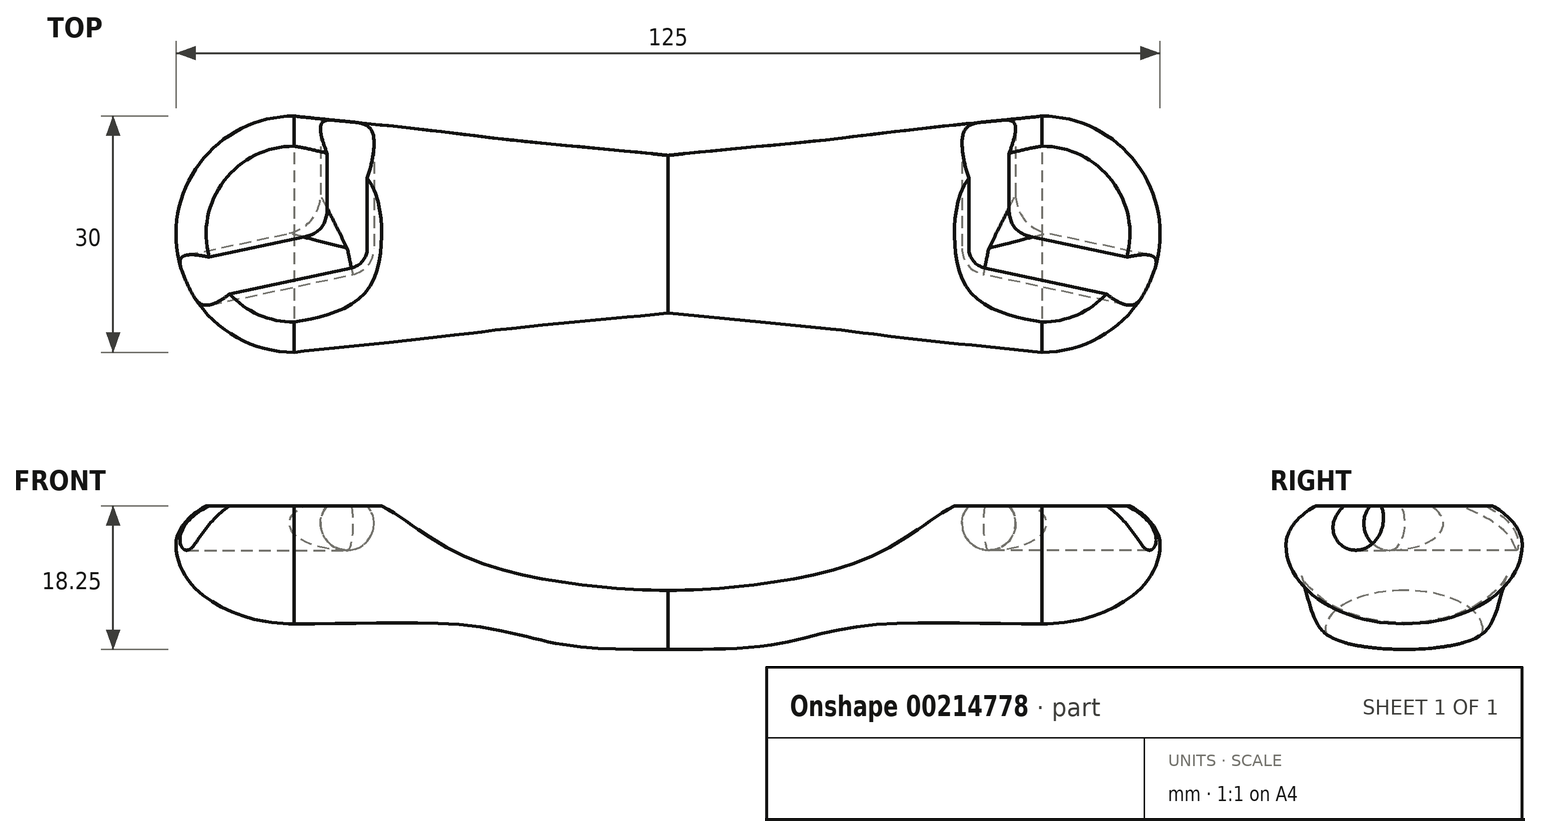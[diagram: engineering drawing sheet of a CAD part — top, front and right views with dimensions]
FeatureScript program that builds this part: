
annotation { "Feature Type Name" : "Feature", "Feature Type Description" : "" }
export const myFeature = defineFeature(function(context is Context, id is Id, definition is map)
    precondition{}
    {
        {
            var Q0;
            Q0=qCreatedBy(makeId("Front.planeOp"),FACE);
            var sketch = newSketch(context, id + "F0", { "sketchPlane" : qUnion([Q0])});
            skLineSegment(sketch, "E0.right", {"start": v(0, -5) * mm, "end": v(0, 0) * mm});
            skLineSegment(sketch, "E1", {"start": v(-66.89, 30) * mm, "end": v(27.85, 30) * mm, "construction": true});
            skEllipticalArc(sketch, "E2", {});
            skEllipticalArc(sketch, "E3", {});
            skLineSegment(sketch, "E4", {"start": v(-47.5, 58.7) * mm, "end": v(-47.5, 14.93) * mm, "construction": true});
            skLineSegment(sketch, "E5", {"start": v(-47.5, 37.5) * mm, "end": v(-47.5, 20) * mm});
            const initialGuessF0  = {"E2": [-0.0475, 0.03, -1, 0, 0.015, 0.01, 0, 3.141592653589793], "E3": [-0.0475, 0.03, 1, 0, 0.015, 0.0075, 0, 3.141592653589793]};
            skSetInitialGuess(sketch, initialGuessF0);
            skSolve(sketch);
        }
        {
            var Q0;
            {var subQ3=sQuery(id+"F0.wireOp",EDGE,"E5");Q0=makeQuery(id+"F0.imprint","IMPRINT",FACE,{"disambiguationData":[TD([[makeQuery(id+"F0.imprint","IMPRINT",EDGE,{"derivedFrom":subQ3}),-1.0]])]});}
            var Q1;
            Q1=sQuery(id+"F0.wireOp",EDGE,"E4");
            revolve(context, id + "F1", {"entities" : qUnion([Q0]), "axis" : qUnion([Q1]), "revolveType" : RevolveType.SYMMETRIC, "angle" : 180 * degree});
        }
        {
            var Q0;
            Q0=qCreatedBy(makeId("Right.planeOp"),FACE);
            var sketch = newSketch(context, id + "F2", { "sketchPlane" : qUnion([Q0])});
            skLineSegment(sketch, "E6", {"start": v(-48.07, 24.25) * mm, "end": v(57.01, 24.25) * mm, "construction": true});
            skEllipticalArc(sketch, "E7", {});
            skEllipticalArc(sketch, "E8", {});
            const initialGuessF2  = {"E7": [0, 0.01925, 1, 0, 0.01, 0.005, 0, 3.141592653589793], "E8": [0, 0.01925, 1, 0, 0.01, 0.0025, 3.141592653589793, 0]};
            skSetInitialGuess(sketch, initialGuessF2);
            skSolve(sketch);
        }
        {
            var Q0;
            Q0=qCreatedBy(makeId("Front.planeOp"),FACE);
            var sketch = newSketch(context, id + "F3", { "sketchPlane" : qUnion([Q0])});
            skLineSegment(sketch, "E9", {"start": v(-68.17, 37.5) * mm, "end": v(-30.06, 37.5) * mm, "construction": true});
            skLineSegment(sketch, "E10", {"start": v(-12.41, 24.25) * mm, "end": v(18, 24.25) * mm, "construction": true});
            skLineSegment(sketch, "E11", {"start": v(-13.42, 16.75) * mm, "end": v(11.03, 16.75) * mm, "construction": true});
            skLineSegment(sketch, "E12", {"start": v(-65.95, 20) * mm, "end": v(-30.87, 20) * mm, "construction": true});
            skLineSegment(sketch, "E13", {"start": v(-47.5, 46.97) * mm, "end": v(-47.5, 9.67) * mm, "construction": true});
            skFitSpline(sketch, "E14", {"points": [v(0, 24.25) * mm, v(-24.74, 28.08) * mm, v(-37.86, 35.73) * mm, v(-47.5, 37.5) * mm], "startDerivative": vector(-40.54, 0) * mm, "endDerivative": vector(-26.76, 0) * mm});
            skFitSpline(sketch, "E15", {"points": [v(0, 16.75) * mm, v(-13.39, 17.37) * mm, v(-24.2, 19.66) * mm, v(-47.5, 20) * mm], "startDerivative": vector(-45.21, 0) * mm, "endDerivative": vector(-63.5, 0) * mm});
            skSolve(sketch);
        }
        {
            var Q1;
            Q1=makeQuery(id+"F2.imprint","IMPRINT",FACE,{"disambiguationData":[TD([[makeQuery(id+"F2.imprint","IMPRINT",EDGE,{"derivedFrom":sQuery(id+"F2.wireOp",EDGE,"E7")}),1.0]])]});
            var Q2;
            Q2=makeQuery(id+"F1.opRevolve","CAP_FACE",FACE,{"disambiguationData":[OSD([sQuery(id+"F0.wireOp",EDGE,"E2"),sQuery(id+"F0.wireOp",EDGE,"E3"),sQuery(id+"F0.wireOp",EDGE,"E5")])],"isStart":false});
            var Q3;
            Q3=sQuery(id+"F3.wireOp",EDGE,"E14");
            var Q4;
            Q4=sQuery(id+"F3.wireOp",EDGE,"E15");
            loft(context, id + "F4", {"operationType" : NewBodyOperationType.ADD, "addGuides" : true, "sheetProfilesArray" : [{ "sheetProfileEntities" : qUnion([Q1]) }, { "sheetProfileEntities" : qUnion([Q2]) }], "guidesArray" : [{ "guideEntities" : qUnion([Q3]), "guideDerivativeType" : LoftGuideDerivativeType.DEFAULT, "guideDerivativeMagnitude" : 1 }, { "guideEntities" : qUnion([Q4]), "guideDerivativeType" : LoftGuideDerivativeType.DEFAULT, "guideDerivativeMagnitude" : 1 }]});
        }
        {
            var Q0;
            Q0=qCreatedBy(makeId("Top.planeOp"),FACE);
            cPlane(context, id + "F5", {"entities" : qUnion([Q0]), "cplaneType" : CPlaneType.OFFSET, "offset" : 32.75 * mm, "width" : 150 * mm, "height" : 150 * mm});
        }
        {
            var Q0;
            Q0=qCreatedBy(id+"F5.planeOp",FACE);
            var sketch = newSketch(context, id + "F6", { "sketchPlane" : qUnion([Q0])});
            skLineSegment(sketch, "E16.bottom", {"start": v(-35, 12.5) * mm, "end": v(-60, 12.5) * mm});
            skLineSegment(sketch, "E16.top", {"start": v(-35, -12.5) * mm, "end": v(-60, -12.5) * mm});
            skLineSegment(sketch, "E16.left", {"start": v(-35, 12.5) * mm, "end": v(-35, -12.5) * mm});
            skLineSegment(sketch, "E16.right", {"start": v(-60, 12.5) * mm, "end": v(-60, -12.5) * mm});
            skPoint(sketch, "E16.middle", {"position": v(-47.5, 0) * mm});
            skLineSegment(sketch, "E17", {"start": v(-40.75, 16.45) * mm, "end": v(-40.75, -7.26) * mm});
            skLineSegment(sketch, "E18", {"start": v(-37, 0) * mm, "end": v(-40.75, 0) * mm});
            skLineSegment(sketch, "E19", {"start": v(-37.35, 16.45) * mm, "end": v(-40.75, 16.45) * mm});
            skPoint(sketch, "E20.start.orphan", {"position": v(-35, -0.5) * mm});
            skLineSegment(sketch, "E21", {"start": v(-64.66, -6.88) * mm, "end": v(-65.36, -3.55) * mm});
            skLineSegment(sketch, "E22", {"start": v(-65.36, -3.55) * mm, "end": v(-41.46, 1.53) * mm});
            skLineSegment(sketch, "E23", {"start": v(-37.35, 16.45) * mm, "end": v(-37.35, -7) * mm});
            skArc(sketch, "E24", {"start": v(-40.75, -5.2) * mm, "mid": v(-37.37, -1.44) * mm, "end": v(-41.46, 1.53) * mm});
            skLineSegment(sketch, "E25.trimOffspring", {"start": v(-37.42, -1.09) * mm, "end": v(-82.55, -10.68) * mm});
            skSolve(sketch);
        }
        {
            var Q0;
            {var subQ5=sQuery(id+"F6.wireOp",EDGE,"E19");Q0=makeQuery(id+"F6.imprint","IMPRINT",FACE,{"disambiguationData":[TD([[makeQuery(id+"F6.imprint","IMPRINT",EDGE,{"derivedFrom":subQ5}),1.0]])]});}
            var Q1;
            {var subQ0=sQuery(id+"F6.wireOp",EDGE,"E23");var subQ1=sQuery(id+"F6.wireOp",EDGE,"E16.bottom");var subQ2=makeQuery(id+"F6.imprint","INTERSECT",VERTEX,{"derivedFrom":[subQ1,subQ0]});Q1=makeQuery(id+"F6.imprint","IMPRINT",FACE,{"disambiguationData":[TD([[makeQuery(id+"F6.imprint","IMPRINT",EDGE,{"disambiguationData":[TD([[subQ2,-1.0]])],"derivedFrom":subQ1}),1.0]])]});}
            var Q2;
            {var subQ0=sQuery(id+"F6.wireOp",EDGE,"E23");var subQ1=sQuery(id+"F6.wireOp",EDGE,"E18");var subQ2=makeQuery(id+"F6.imprint","INTERSECT",VERTEX,{"derivedFrom":[subQ1,subQ0]});Q2=makeQuery(id+"F6.imprint","IMPRINT",FACE,{"disambiguationData":[TD([[makeQuery(id+"F6.imprint","IMPRINT",EDGE,{"disambiguationData":[TD([[subQ2,-1.0]])],"derivedFrom":subQ1}),1.0]])]});}
            var Q3;
            {var subQ0=sQuery(id+"F6.wireOp",EDGE,"E18");var subQ1=sQuery(id+"F6.wireOp",EDGE,"E17");var subQ2=makeQuery(id+"F6.imprint","INTERSECT",VERTEX,{"derivedFrom":[subQ1,subQ0]});Q3=makeQuery(id+"F6.imprint","IMPRINT",FACE,{"disambiguationData":[TD([[makeQuery(id+"F6.imprint","IMPRINT",EDGE,{"disambiguationData":[TD([[subQ2,-1.0]])],"derivedFrom":subQ1}),1.0]])]});}
            var Q4;
            {var subQ0=sQuery(id+"F6.wireOp",EDGE,"E18");var subQ1=sQuery(id+"F6.wireOp",EDGE,"E17");var subQ2=makeQuery(id+"F6.imprint","INTERSECT",VERTEX,{"derivedFrom":[subQ1,subQ0]});Q4=makeQuery(id+"F6.imprint","IMPRINT",FACE,{"disambiguationData":[TD([[makeQuery(id+"F6.imprint","IMPRINT",EDGE,{"disambiguationData":[TD([[subQ2,1.0]])],"derivedFrom":subQ1}),1.0]])]});}
            var Q5;
            {var subQ0=sQuery(id+"F6.wireOp",EDGE,"E24");var subQ1=sQuery(id+"F6.wireOp",EDGE,"E17");var subQ2=makeQuery(id+"F6.imprint","INTERSECT",VERTEX,{"disambiguationData":[OD(0.0)],"derivedFrom":[subQ1,subQ0]});Q5=makeQuery(id+"F6.imprint","IMPRINT",FACE,{"disambiguationData":[TD([[makeQuery(id+"F6.imprint","IMPRINT",EDGE,{"disambiguationData":[TD([[subQ2,1.0]])],"derivedFrom":subQ1}),1.0]])]});}
            var Q6;
            Q6=sQuery(id+"F6.wireOp",EDGE,"E17");
            revolve(context, id + "F7", {"operationType" : NewBodyOperationType.REMOVE, "entities" : qUnion([Q0, Q1, Q2, Q3, Q4, Q5]), "axis" : qUnion([Q6]), "revolveType" : RevolveType.FULL, "oppositeDirection" : true});
        }
        {
            var Q0;
            {var subQ5=sQuery(id+"F6.wireOp",EDGE,"E21");Q0=makeQuery(id+"F6.imprint","IMPRINT",FACE,{"disambiguationData":[TD([[makeQuery(id+"F6.imprint","IMPRINT",EDGE,{"derivedFrom":subQ5}),-1.0]])]});}
            var Q1;
            {var subQ1=sQuery(id+"F6.wireOp",EDGE,"E22");var subQ3=sQuery(id+"F6.wireOp",EDGE,"E16.right");var subQ4=makeQuery(id+"F6.imprint","INTERSECT",VERTEX,{"derivedFrom":[subQ3,subQ1]});Q1=makeQuery(id+"F6.imprint","IMPRINT",FACE,{"disambiguationData":[TD([[makeQuery(id+"F6.imprint","IMPRINT",EDGE,{"disambiguationData":[TD([[subQ4,-1.0]])],"derivedFrom":subQ3}),1.0]])]});}
            var Q2;
            {var subQ0=sQuery(id+"F6.wireOp",EDGE,"E18");var subQ1=sQuery(id+"F6.wireOp",EDGE,"E17");var subQ2=makeQuery(id+"F6.imprint","INTERSECT",VERTEX,{"derivedFrom":[subQ1,subQ0]});Q2=makeQuery(id+"F6.imprint","IMPRINT",FACE,{"disambiguationData":[TD([[makeQuery(id+"F6.imprint","IMPRINT",EDGE,{"disambiguationData":[TD([[subQ2,-1.0]])],"derivedFrom":subQ1}),1.0]])]});}
            var Q3;
            {var subQ0=sQuery(id+"F6.wireOp",EDGE,"E18");var subQ1=sQuery(id+"F6.wireOp",EDGE,"E17");var subQ2=makeQuery(id+"F6.imprint","INTERSECT",VERTEX,{"derivedFrom":[subQ1,subQ0]});Q3=makeQuery(id+"F6.imprint","IMPRINT",FACE,{"disambiguationData":[TD([[makeQuery(id+"F6.imprint","IMPRINT",EDGE,{"disambiguationData":[TD([[subQ2,1.0]])],"derivedFrom":subQ1}),1.0]])]});}
            var Q4;
            Q4=sQuery(id+"F6.wireOp",EDGE,"E25.trimOffspring");
            revolve(context, id + "F8", {"operationType" : NewBodyOperationType.REMOVE, "entities" : qUnion([Q0, Q1, Q2, Q3]), "axis" : qUnion([Q4]), "revolveType" : RevolveType.FULL});
        }
        {
            var Q0;
            Q0=qCreatedBy(makeId("Front.planeOp"),FACE);
            var sketch = newSketch(context, id + "F9", { "sketchPlane" : qUnion([Q0])});
            skLineSegment(sketch, "E26.bottom", {"start": v(-29.95, 35) * mm, "end": v(-64.95, 35) * mm});
            skLineSegment(sketch, "E26.top", {"start": v(-29.95, 50) * mm, "end": v(-64.95, 50) * mm});
            skLineSegment(sketch, "E26.left", {"start": v(-29.95, 35) * mm, "end": v(-29.95, 50) * mm});
            skLineSegment(sketch, "E26.right", {"start": v(-64.95, 35) * mm, "end": v(-64.95, 50) * mm});
            skPoint(sketch, "E26.middle", {"position": v(-47.45, 42.5) * mm});
            skSolve(sketch);
        }
        {
            var Q0;
            Q0=makeQuery(id+"F9.imprint","IMPRINT",FACE,{"disambiguationData":[TD([[makeQuery(id+"F9.imprint","IMPRINT",EDGE,{"derivedFrom":sQuery(id+"F9.wireOp",EDGE,"E26.bottom")}),-1.0]])]});
            extrude(context, id + "F10", {"entities" : qUnion([Q0]), "operationType" : NewBodyOperationType.REMOVE, "endBound" : BoundingType.SYMMETRIC, "oppositeDirection" : true, "depth" : 25 * mm});
        }
        {
            var Q0;
            Q0=makeQuery(id+"F8.boolean.opBoolean","INTERSECT",EDGE,{"derivedFrom":[makeQuery(id+"F7.boolean.opBoolean","COPY",FACE,{"derivedFrom":makeQuery(id+"F7.opRevolve","SWEPT_FACE",FACE,{"disambiguationData":[OSD([sQuery(id+"F6.wireOp",EDGE,"E23")])]})}),makeQuery(id+"F8.opRevolve","SWEPT_FACE",FACE,{"disambiguationData":[OSD([sQuery(id+"F6.wireOp",EDGE,"E22")])]})]});
            fillet(context, id + "F11", {"entities" : qUnion([Q0]), "radius" : 5 * mm, "tangentPropagation" : true, "allowEdgeOverflow" : false});
        }
        {
            var Q0;
            Q0=makeQuery(id+"F1.opRevolve","SWEPT_BODY",BODY,{"disambiguationData":[OSD([sQuery(id+"F0.wireOp",EDGE,"E2"),sQuery(id+"F0.wireOp",EDGE,"E3"),sQuery(id+"F0.wireOp",EDGE,"E5")])]});
            var Q1;
            Q1=qCreatedBy(makeId("Right.planeOp"),FACE);
            mirror(context, id + "F12", {"operationType" : NewBodyOperationType.ADD, "entities" : qUnion([Q0]), "mirrorPlane" : qUnion([Q1])});
        }
    });
